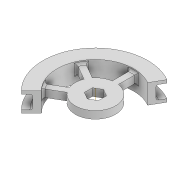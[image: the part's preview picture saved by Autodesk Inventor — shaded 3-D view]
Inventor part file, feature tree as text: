
AUTODESK INVENTOR PART (.ipt)
format: ipt  version: 2022 (Build 260153000, 153)  size: 236,032 bytes
history: native  units: mm
features: extrude x7, sketch x7, projected_geometry x4, fillet x2
ambient origin geometry x8: Origin, YZ Plane, XZ Plane, XY Plane, X Axis, Y Axis, Z Axis, Center Point
bodies: Solid1 (feature_tree)
feature tree (20):
  extrude  "Extrusion1"  Depth=44.0mm
  extrude  "Extrusion4"  Depth=4.0mm
  extrude  "Extrusion10"  Depth=1.5mm TaperAngle=0.0deg
  extrude  "Extrusion5"  Depth=20.0mm
  extrude  "Extrusion7"  Depth=1.5mm
  extrude  "Extrusion8"  Depth=10.0mm TaperAngle=0.0deg
  fillet  "Fillet1"  Radius=7.0mm
  extrude  "Extrusion9"  Depth=1.0mm
  fillet  "Fillet2"  [1 undecoded]
  sketch  "Sketch1"  dims[d0=4.1mm d1=44.0mm]
  sketch  "Sketch5"  dims[d2=3.7mm d3=0.0mm d11=4.0mm]
  projected_geometry  "Projected Loop4"
  sketch  "Sketch6"  dims[d12=1.5mm d13=0.0mm d15=1.5mm d16=0.0mm]
  projected_geometry  "Projected Loop5"
  sketch  "Sketch7"  dims[d17=3.0mm d19=20.0mm]
  projected_geometry  "Projected Loop6"
  sketch  "Sketch8"  dims[d20=3.0mm d21=1.5mm]
  sketch  "Sketch9"  dims[d24=60.0mm d26=360.0deg d28=10.0mm d29=0.0mm d30=7.0mm]
  sketch  "Sketch11"  dims[d31=10.0mm d32=0.0mm d33=1.0mm d34=150.0deg d35=45.0deg d36=10.0mm d37=0.0mm d38=3.0mm d39=3.0mm d40=0.0mm d41=20.0mm d42=1.0mm]
  projected_geometry  "Projected Loop7"
note: 1 required parameter value undecoded (feature->parameter linkage not recoverable at this tier; creation-order binding heuristic only, values carry confidence <= 0.55)
